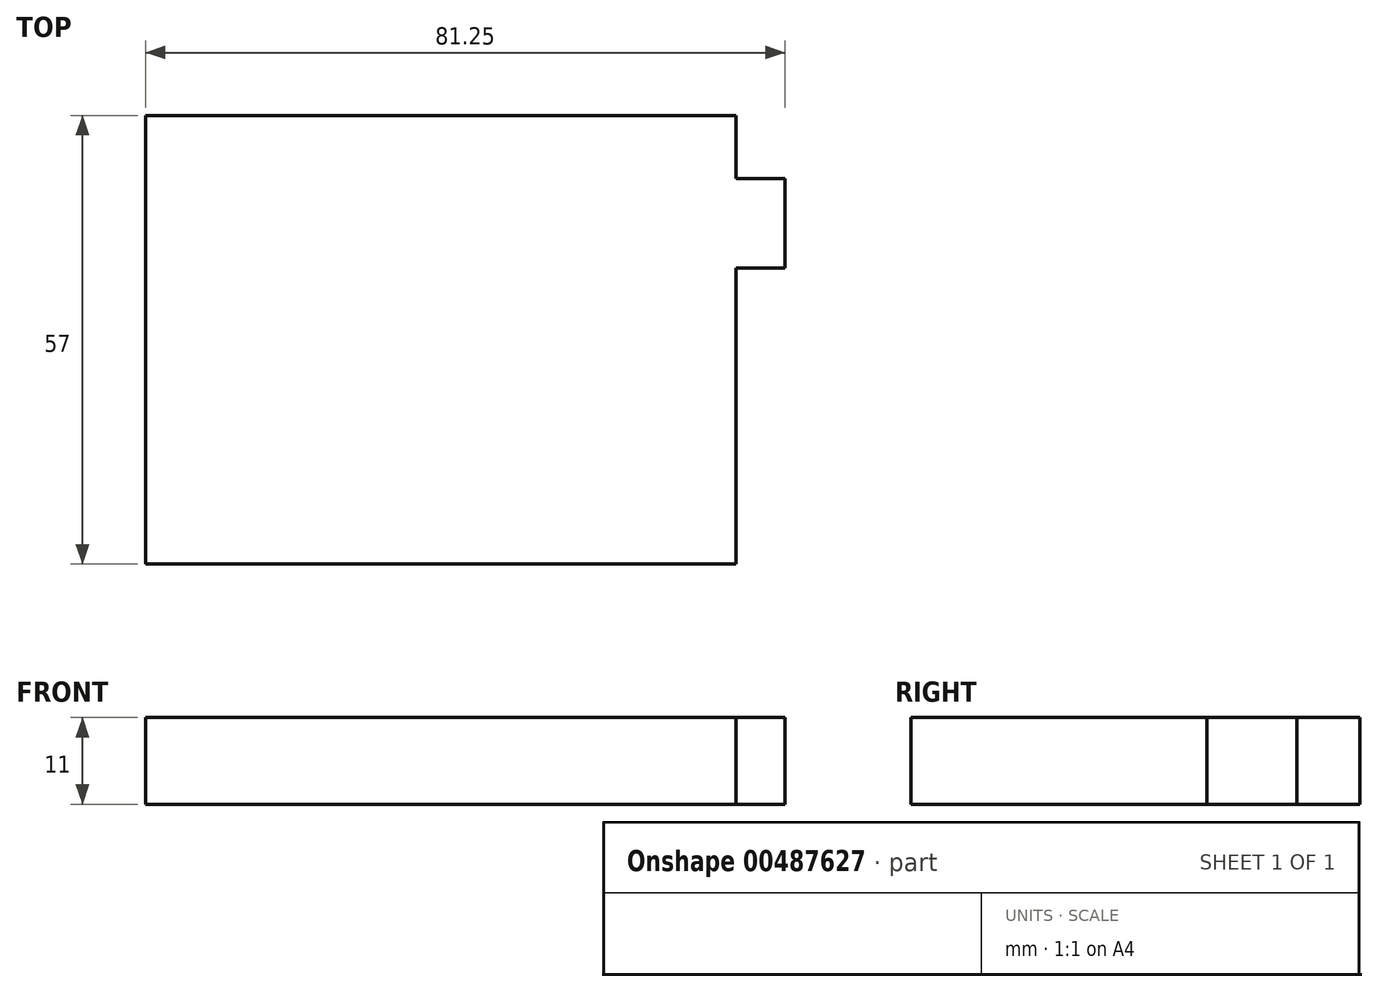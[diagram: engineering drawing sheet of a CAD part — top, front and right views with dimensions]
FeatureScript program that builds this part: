
annotation { "Feature Type Name" : "Feature", "Feature Type Description" : "" }
export const myFeature = defineFeature(function(context is Context, id is Id, definition is map)
    precondition{}
    {
        {
            var Q0;
            Q0=qCreatedBy(makeId("Top.planeOp"),FACE);
            var sketch = newSketch(context, id + "F0", { "sketchPlane" : qUnion([Q0])});
            skLineSegment(sketch, "E0.bottom", {"start": v(37.5, -28.5) * mm, "end": v(-37.5, -28.5) * mm});
            skLineSegment(sketch, "E0.top", {"start": v(37.5, 28.5) * mm, "end": v(-37.5, 28.5) * mm});
            skLineSegment(sketch, "E0.left", {"start": v(37.5, -28.5) * mm, "end": v(37.5, 28.5) * mm});
            skLineSegment(sketch, "E0.right", {"start": v(-37.5, -28.5) * mm, "end": v(-37.5, 28.5) * mm});
            skPoint(sketch, "E0.middle", {"position": v(0, 0) * mm});
            skLineSegment(sketch, "E1.bottom", {"start": v(43.75, 9.1) * mm, "end": v(31.25, 9.1) * mm});
            skLineSegment(sketch, "E1.top", {"start": v(43.75, 20.5) * mm, "end": v(31.25, 20.5) * mm});
            skLineSegment(sketch, "E1.left", {"start": v(43.75, 9.1) * mm, "end": v(43.75, 20.5) * mm});
            skLineSegment(sketch, "E1.right", {"start": v(31.25, 9.1) * mm, "end": v(31.25, 20.5) * mm});
            skPoint(sketch, "E1.middle", {"position": v(37.5, 14.8) * mm});
            skSolve(sketch);
        }
        {
            var Q0;
            {var subQ4=sQuery(id+"F0.wireOp",EDGE,"E0.bottom");Q0=makeQuery(id+"F0.imprint","IMPRINT",FACE,{"disambiguationData":[TD([[makeQuery(id+"F0.imprint","IMPRINT",EDGE,{"derivedFrom":subQ4}),-1.0]])]});}
            var Q1;
            {var subQ5=sQuery(id+"F0.wireOp",EDGE,"E1.right");Q1=makeQuery(id+"F0.imprint","IMPRINT",FACE,{"disambiguationData":[TD([[makeQuery(id+"F0.imprint","IMPRINT",EDGE,{"derivedFrom":subQ5}),-1.0]])]});}
            var Q2;
            {var subQ5=sQuery(id+"F0.wireOp",EDGE,"E1.left");Q2=makeQuery(id+"F0.imprint","IMPRINT",FACE,{"disambiguationData":[TD([[makeQuery(id+"F0.imprint","IMPRINT",EDGE,{"derivedFrom":subQ5}),1.0]])]});}
            extrude(context, id + "F1", {"entities" : qUnion([Q0, Q1, Q2]), "depth" : 11 * mm});
        }
    });
